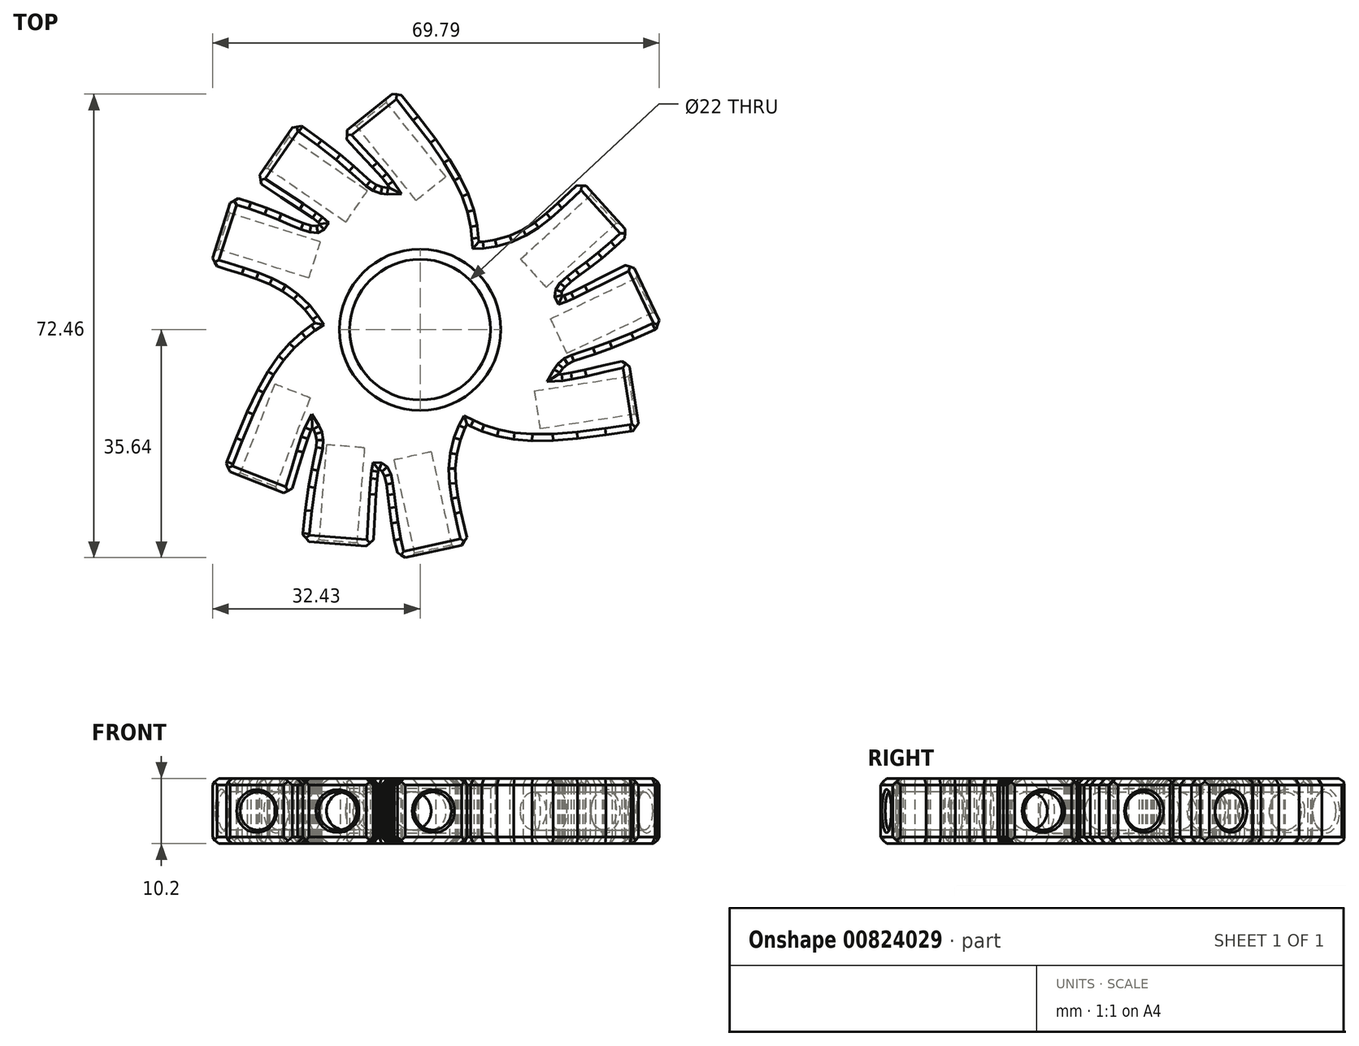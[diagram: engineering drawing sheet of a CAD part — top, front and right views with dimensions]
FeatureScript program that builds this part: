
annotation { "Feature Type Name" : "Feature", "Feature Type Description" : "" }
export const myFeature = defineFeature(function(context is Context, id is Id, definition is map)
    precondition{}
    {
        {
            var Q0;
            Q0=qCreatedBy(makeId("Top.planeOp"),FACE);
            var sketch = newSketch(context, id + "F0", { "sketchPlane" : qUnion([Q0])});
            skLineSegment(sketch, "E0", {"start": v(-3.87, -42.17) * mm, "end": v(8.83, -39.4) * mm});
            skLineSegment(sketch, "E1", {"start": v(8.83, -39.4) * mm, "end": v(8.67, -38.64) * mm});
            skLineSegment(sketch, "E2", {"start": v(8.67, -38.64) * mm, "end": v(8.17, -36.4) * mm});
            skLineSegment(sketch, "E3", {"start": v(8.17, -36.4) * mm, "end": v(7.52, -33.55) * mm});
            skLineSegment(sketch, "E4", {"start": v(7.52, -33.55) * mm, "end": v(6.96, -30.83) * mm});
            skLineSegment(sketch, "E5", {"start": v(6.96, -30.83) * mm, "end": v(6.6, -28.19) * mm});
            skLineSegment(sketch, "E6", {"start": v(6.6, -28.19) * mm, "end": v(6.48, -25.57) * mm});
            skLineSegment(sketch, "E7", {"start": v(6.48, -25.57) * mm, "end": v(6.72, -22.93) * mm});
            skLineSegment(sketch, "E8", {"start": v(6.72, -22.93) * mm, "end": v(7.4, -20.23) * mm});
            skLineSegment(sketch, "E9", {"start": v(7.4, -20.23) * mm, "end": v(8.24, -18.1) * mm});
            skLineSegment(sketch, "E10", {"start": v(8.24, -18.1) * mm, "end": v(8.6, -17.42) * mm});
            skLineSegment(sketch, "E11", {"start": v(8.6, -17.42) * mm, "end": v(9.26, -17.76) * mm});
            skLineSegment(sketch, "E12", {"start": v(9.26, -17.76) * mm, "end": v(11.34, -18.65) * mm});
            skLineSegment(sketch, "E13", {"start": v(11.34, -18.65) * mm, "end": v(14.16, -19.56) * mm});
            skLineSegment(sketch, "E14", {"start": v(14.16, -19.56) * mm, "end": v(17.2, -20.15) * mm});
            skLineSegment(sketch, "E15", {"start": v(17.2, -20.15) * mm, "end": v(20.6, -20.42) * mm});
            skLineSegment(sketch, "E16", {"start": v(20.6, -20.42) * mm, "end": v(24.46, -20.37) * mm});
            skLineSegment(sketch, "E17", {"start": v(24.46, -20.37) * mm, "end": v(28.95, -20.02) * mm});
            skLineSegment(sketch, "E18", {"start": v(28.95, -20.02) * mm, "end": v(34.19, -19.35) * mm});
            skLineSegment(sketch, "E19", {"start": v(34.19, -19.35) * mm, "end": v(38.78, -18.65) * mm});
            skLineSegment(sketch, "E20", {"start": v(38.78, -18.65) * mm, "end": v(40.3, -18.39) * mm});
            skLineSegment(sketch, "E21", {"start": v(40.3, -18.39) * mm, "end": v(38.33, -5.54) * mm});
            skLineSegment(sketch, "E22", {"start": v(38.33, -5.54) * mm, "end": v(37.16, -5.78) * mm});
            skLineSegment(sketch, "E23", {"start": v(37.16, -5.78) * mm, "end": v(33.7, -6.57) * mm});
            skLineSegment(sketch, "E24", {"start": v(33.7, -6.57) * mm, "end": v(30.3, -7.38) * mm});
            skLineSegment(sketch, "E25", {"start": v(30.3, -7.38) * mm, "end": v(27.7, -7.94) * mm});
            skLineSegment(sketch, "E26", {"start": v(27.7, -7.94) * mm, "end": v(26.02, -8.19) * mm});
            skLineSegment(sketch, "E27", {"start": v(26.02, -8.19) * mm, "end": v(25.45, -8.22) * mm});
            skLineSegment(sketch, "E28", {"start": v(25.45, -8.22) * mm, "end": v(25.62, -7.92) * mm});
            skLineSegment(sketch, "E29", {"start": v(25.62, -7.92) * mm, "end": v(26.22, -7.09) * mm});
            skLineSegment(sketch, "E30", {"start": v(26.22, -7.09) * mm, "end": v(27.1, -6.34) * mm});
            skLineSegment(sketch, "E31", {"start": v(27.1, -6.34) * mm, "end": v(28.29, -5.78) * mm});
            skLineSegment(sketch, "E32", {"start": v(28.29, -5.78) * mm, "end": v(29.92, -5.22) * mm});
            skLineSegment(sketch, "E33", {"start": v(29.92, -5.22) * mm, "end": v(32.2, -4.48) * mm});
            skLineSegment(sketch, "E34", {"start": v(32.2, -4.48) * mm, "end": v(35.26, -3.38) * mm});
            skLineSegment(sketch, "E35", {"start": v(35.26, -3.38) * mm, "end": v(39.3, -1.73) * mm});
            skLineSegment(sketch, "E36", {"start": v(39.3, -1.73) * mm, "end": v(43.18, 0.04) * mm});
            skLineSegment(sketch, "E37", {"start": v(43.18, 0.04) * mm, "end": v(44.46, 0.66) * mm});
            skLineSegment(sketch, "E38", {"start": v(44.46, 0.66) * mm, "end": v(38.88, 12.4) * mm});
            skLineSegment(sketch, "E39", {"start": v(38.88, 12.4) * mm, "end": v(37.64, 11.78) * mm});
            skLineSegment(sketch, "E40", {"start": v(37.64, 11.78) * mm, "end": v(33.94, 9.92) * mm});
            skLineSegment(sketch, "E41", {"start": v(33.94, 9.92) * mm, "end": v(30.3, 8.08) * mm});
            skLineSegment(sketch, "E42", {"start": v(30.3, 8.08) * mm, "end": v(27.73, 6.83) * mm});
            skLineSegment(sketch, "E43", {"start": v(27.73, 6.83) * mm, "end": v(26.49, 6.28) * mm});
            skLineSegment(sketch, "E44", {"start": v(26.49, 6.28) * mm, "end": v(26.06, 6.14) * mm});
            skLineSegment(sketch, "E45", {"start": v(26.06, 6.14) * mm, "end": v(25.98, 6.3) * mm});
            skLineSegment(sketch, "E46", {"start": v(25.98, 6.3) * mm, "end": v(26.03, 6.93) * mm});
            skLineSegment(sketch, "E47", {"start": v(26.03, 6.93) * mm, "end": v(26.62, 7.8) * mm});
            skLineSegment(sketch, "E48", {"start": v(26.62, 7.8) * mm, "end": v(27.73, 8.8) * mm});
            skLineSegment(sketch, "E49", {"start": v(27.73, 8.8) * mm, "end": v(29.3, 10) * mm});
            skLineSegment(sketch, "E50", {"start": v(29.3, 10) * mm, "end": v(31.24, 11.44) * mm});
            skLineSegment(sketch, "E51", {"start": v(31.24, 11.44) * mm, "end": v(33.46, 13.17) * mm});
            skLineSegment(sketch, "E52", {"start": v(33.46, 13.17) * mm, "end": v(35.89, 15.24) * mm});
            skLineSegment(sketch, "E53", {"start": v(35.89, 15.24) * mm, "end": v(37.83, 17.06) * mm});
            skLineSegment(sketch, "E54", {"start": v(37.83, 17.06) * mm, "end": v(38.44, 17.7) * mm});
            skLineSegment(sketch, "E55", {"start": v(38.44, 17.7) * mm, "end": v(29.69, 27.3) * mm});
            skLineSegment(sketch, "E56", {"start": v(29.69, 27.3) * mm, "end": v(29.11, 26.8) * mm});
            skLineSegment(sketch, "E57", {"start": v(29.11, 26.8) * mm, "end": v(27.42, 25.23) * mm});
            skLineSegment(sketch, "E58", {"start": v(27.42, 25.23) * mm, "end": v(25.28, 23.25) * mm});
            skLineSegment(sketch, "E59", {"start": v(25.28, 23.25) * mm, "end": v(23.2, 21.41) * mm});
            skLineSegment(sketch, "E60", {"start": v(23.2, 21.41) * mm, "end": v(21.1, 19.77) * mm});
            skLineSegment(sketch, "E61", {"start": v(21.1, 19.77) * mm, "end": v(18.89, 18.37) * mm});
            skLineSegment(sketch, "E62", {"start": v(18.89, 18.37) * mm, "end": v(16.48, 17.26) * mm});
            skLineSegment(sketch, "E63", {"start": v(16.48, 17.26) * mm, "end": v(13.8, 16.5) * mm});
            skLineSegment(sketch, "E64", {"start": v(13.8, 16.5) * mm, "end": v(11.53, 16.15) * mm});
            skLineSegment(sketch, "E65", {"start": v(11.53, 16.15) * mm, "end": v(10.77, 16.12) * mm});
            skLineSegment(sketch, "E66", {"start": v(10.77, 16.12) * mm, "end": v(10.73, 16.87) * mm});
            skLineSegment(sketch, "E67", {"start": v(10.73, 16.87) * mm, "end": v(10.47, 19.11) * mm});
            skLineSegment(sketch, "E68", {"start": v(10.47, 19.11) * mm, "end": v(9.84, 22.01) * mm});
            skLineSegment(sketch, "E69", {"start": v(9.84, 22.01) * mm, "end": v(8.83, 24.94) * mm});
            skLineSegment(sketch, "E70", {"start": v(8.83, 24.94) * mm, "end": v(7.37, 28) * mm});
            skLineSegment(sketch, "E71", {"start": v(7.37, 28) * mm, "end": v(5.4, 31.34) * mm});
            skLineSegment(sketch, "E72", {"start": v(5.4, 31.34) * mm, "end": v(2.84, 35.05) * mm});
            skLineSegment(sketch, "E73", {"start": v(2.84, 35.05) * mm, "end": v(-0.35, 39.25) * mm});
            skLineSegment(sketch, "E74", {"start": v(-0.35, 39.25) * mm, "end": v(-3.26, 42.87) * mm});
            skLineSegment(sketch, "E75", {"start": v(-3.26, 42.87) * mm, "end": v(-4.24, 44.06) * mm});
            skLineSegment(sketch, "E76", {"start": v(-4.24, 44.06) * mm, "end": v(-14.38, 35.92) * mm});
            skLineSegment(sketch, "E77", {"start": v(-14.38, 35.92) * mm, "end": v(-13.6, 35.04) * mm});
            skLineSegment(sketch, "E78", {"start": v(-13.6, 35.04) * mm, "end": v(-11.17, 32.43) * mm});
            skLineSegment(sketch, "E79", {"start": v(-11.17, 32.43) * mm, "end": v(-8.77, 29.9) * mm});
            skLineSegment(sketch, "E80", {"start": v(-8.77, 29.9) * mm, "end": v(-7, 27.93) * mm});
            skLineSegment(sketch, "E81", {"start": v(-7, 27.93) * mm, "end": v(-5.94, 26.59) * mm});
            skLineSegment(sketch, "E82", {"start": v(-5.94, 26.59) * mm, "end": v(-5.63, 26.11) * mm});
            skLineSegment(sketch, "E83", {"start": v(-5.63, 26.11) * mm, "end": v(-5.97, 26.1) * mm});
            skLineSegment(sketch, "E84", {"start": v(-5.97, 26.1) * mm, "end": v(-6.99, 26.21) * mm});
            skLineSegment(sketch, "E85", {"start": v(-6.99, 26.21) * mm, "end": v(-8.08, 26.6) * mm});
            skLineSegment(sketch, "E86", {"start": v(-8.08, 26.6) * mm, "end": v(-9.16, 27.35) * mm});
            skLineSegment(sketch, "E87", {"start": v(-9.16, 27.35) * mm, "end": v(-10.46, 28.5) * mm});
            skLineSegment(sketch, "E88", {"start": v(-10.46, 28.5) * mm, "end": v(-12.23, 30.09) * mm});
            skLineSegment(sketch, "E89", {"start": v(-12.23, 30.09) * mm, "end": v(-14.72, 32.2) * mm});
            skLineSegment(sketch, "E90", {"start": v(-14.72, 32.2) * mm, "end": v(-18.17, 34.86) * mm});
            skLineSegment(sketch, "E91", {"start": v(-18.17, 34.86) * mm, "end": v(-21.64, 37.35) * mm});
            skLineSegment(sketch, "E92", {"start": v(-21.64, 37.35) * mm, "end": v(-22.82, 38.14) * mm});
            skLineSegment(sketch, "E93", {"start": v(-22.82, 38.14) * mm, "end": v(-30.2, 27.43) * mm});
            skLineSegment(sketch, "E94", {"start": v(-30.2, 27.43) * mm, "end": v(-29.04, 26.67) * mm});
            skLineSegment(sketch, "E95", {"start": v(-29.04, 26.67) * mm, "end": v(-25.58, 24.4) * mm});
            skLineSegment(sketch, "E96", {"start": v(-25.58, 24.4) * mm, "end": v(-22.16, 22.16) * mm});
            skLineSegment(sketch, "E97", {"start": v(-22.16, 22.16) * mm, "end": v(-19.8, 20.56) * mm});
            skLineSegment(sketch, "E98", {"start": v(-19.8, 20.56) * mm, "end": v(-18.7, 19.76) * mm});
            skLineSegment(sketch, "E99", {"start": v(-18.7, 19.76) * mm, "end": v(-18.36, 19.46) * mm});
            skLineSegment(sketch, "E100", {"start": v(-18.36, 19.46) * mm, "end": v(-18.46, 19.31) * mm});
            skLineSegment(sketch, "E101", {"start": v(-18.46, 19.31) * mm, "end": v(-19.03, 19.04) * mm});
            skLineSegment(sketch, "E102", {"start": v(-19.03, 19.04) * mm, "end": v(-20.08, 19.11) * mm});
            skLineSegment(sketch, "E103", {"start": v(-20.08, 19.11) * mm, "end": v(-21.51, 19.58) * mm});
            skLineSegment(sketch, "E104", {"start": v(-21.51, 19.58) * mm, "end": v(-23.33, 20.34) * mm});
            skLineSegment(sketch, "E105", {"start": v(-23.33, 20.34) * mm, "end": v(-25.54, 21.3) * mm});
            skLineSegment(sketch, "E106", {"start": v(-25.54, 21.3) * mm, "end": v(-28.15, 22.36) * mm});
            skLineSegment(sketch, "E107", {"start": v(-28.15, 22.36) * mm, "end": v(-31.16, 23.43) * mm});
            skLineSegment(sketch, "E108", {"start": v(-31.16, 23.43) * mm, "end": v(-33.7, 24.2) * mm});
            skLineSegment(sketch, "E109", {"start": v(-33.7, 24.2) * mm, "end": v(-34.56, 24.4) * mm});
            skLineSegment(sketch, "E110", {"start": v(-34.56, 24.4) * mm, "end": v(-38.5, 12.02) * mm});
            skLineSegment(sketch, "E111", {"start": v(-38.5, 12.02) * mm, "end": v(-37.78, 11.78) * mm});
            skLineSegment(sketch, "E112", {"start": v(-37.78, 11.78) * mm, "end": v(-35.58, 11.1) * mm});
            skLineSegment(sketch, "E113", {"start": v(-35.58, 11.1) * mm, "end": v(-32.8, 10.23) * mm});
            skLineSegment(sketch, "E114", {"start": v(-32.8, 10.23) * mm, "end": v(-30.16, 9.35) * mm});
            skLineSegment(sketch, "E115", {"start": v(-30.16, 9.35) * mm, "end": v(-27.69, 8.35) * mm});
            skLineSegment(sketch, "E116", {"start": v(-27.69, 8.35) * mm, "end": v(-25.36, 7.14) * mm});
            skLineSegment(sketch, "E117", {"start": v(-25.36, 7.14) * mm, "end": v(-23.2, 5.61) * mm});
            skLineSegment(sketch, "E118", {"start": v(-23.2, 5.61) * mm, "end": v(-21.2, 3.68) * mm});
            skLineSegment(sketch, "E119", {"start": v(-21.2, 3.68) * mm, "end": v(-19.77, 1.88) * mm});
            skLineSegment(sketch, "E120", {"start": v(-19.77, 1.88) * mm, "end": v(-19.36, 1.24) * mm});
            skLineSegment(sketch, "E121", {"start": v(-19.36, 1.24) * mm, "end": v(-20, 0.83) * mm});
            skLineSegment(sketch, "E122", {"start": v(-20, 0.83) * mm, "end": v(-21.8, -0.52) * mm});
            skLineSegment(sketch, "E123", {"start": v(-21.8, -0.52) * mm, "end": v(-24, -2.52) * mm});
            skLineSegment(sketch, "E124", {"start": v(-24, -2.52) * mm, "end": v(-26.03, -4.86) * mm});
            skLineSegment(sketch, "E125", {"start": v(-26.03, -4.86) * mm, "end": v(-27.96, -7.66) * mm});
            skLineSegment(sketch, "E126", {"start": v(-27.96, -7.66) * mm, "end": v(-29.85, -11.03) * mm});
            skLineSegment(sketch, "E127", {"start": v(-29.85, -11.03) * mm, "end": v(-31.79, -15.1) * mm});
            skLineSegment(sketch, "E128", {"start": v(-31.79, -15.1) * mm, "end": v(-33.83, -19.96) * mm});
            skLineSegment(sketch, "E129", {"start": v(-33.83, -19.96) * mm, "end": v(-35.51, -24.3) * mm});
            skLineSegment(sketch, "E130", {"start": v(-35.51, -24.3) * mm, "end": v(-36.05, -25.74) * mm});
            skLineSegment(sketch, "E131", {"start": v(-36.05, -25.74) * mm, "end": v(-23.94, -30.45) * mm});
            skLineSegment(sketch, "E132", {"start": v(-23.94, -30.45) * mm, "end": v(-23.57, -29.33) * mm});
            skLineSegment(sketch, "E133", {"start": v(-23.57, -29.33) * mm, "end": v(-22.52, -25.92) * mm});
            skLineSegment(sketch, "E134", {"start": v(-22.52, -25.92) * mm, "end": v(-21.52, -22.58) * mm});
            skLineSegment(sketch, "E135", {"start": v(-21.52, -22.58) * mm, "end": v(-20.7, -20.06) * mm});
            skLineSegment(sketch, "E136", {"start": v(-20.7, -20.06) * mm, "end": v(-20.07, -18.47) * mm});
            skLineSegment(sketch, "E137", {"start": v(-20.07, -18.47) * mm, "end": v(-19.82, -17.97) * mm});
            skLineSegment(sketch, "E138", {"start": v(-19.82, -17.97) * mm, "end": v(-19.64, -18.26) * mm});
            skLineSegment(sketch, "E139", {"start": v(-19.64, -18.26) * mm, "end": v(-19.23, -19.2) * mm});
            skLineSegment(sketch, "E140", {"start": v(-19.23, -19.2) * mm, "end": v(-19.02, -20.34) * mm});
            skLineSegment(sketch, "E141", {"start": v(-19.02, -20.34) * mm, "end": v(-19.12, -21.64) * mm});
            skLineSegment(sketch, "E142", {"start": v(-19.12, -21.64) * mm, "end": v(-19.46, -23.34) * mm});
            skLineSegment(sketch, "E143", {"start": v(-19.46, -23.34) * mm, "end": v(-19.96, -25.67) * mm});
            skLineSegment(sketch, "E144", {"start": v(-19.96, -25.67) * mm, "end": v(-20.53, -28.88) * mm});
            skLineSegment(sketch, "E145", {"start": v(-20.53, -28.88) * mm, "end": v(-21.12, -33.2) * mm});
            skLineSegment(sketch, "E146", {"start": v(-21.12, -33.2) * mm, "end": v(-21.54, -37.45) * mm});
            skLineSegment(sketch, "E147", {"start": v(-21.54, -37.45) * mm, "end": v(-21.64, -38.87) * mm});
            skLineSegment(sketch, "E148", {"start": v(-21.64, -38.87) * mm, "end": v(-8.68, -39.9) * mm});
            skLineSegment(sketch, "E149", {"start": v(-8.68, -39.9) * mm, "end": v(-8.6, -38.52) * mm});
            skLineSegment(sketch, "E150", {"start": v(-8.6, -38.52) * mm, "end": v(-8.36, -34.39) * mm});
            skLineSegment(sketch, "E151", {"start": v(-8.36, -34.39) * mm, "end": v(-8.13, -30.3) * mm});
            skLineSegment(sketch, "E152", {"start": v(-8.13, -30.3) * mm, "end": v(-7.92, -27.46) * mm});
            skLineSegment(sketch, "E153", {"start": v(-7.92, -27.46) * mm, "end": v(-7.78, -26.11) * mm});
            skLineSegment(sketch, "E154", {"start": v(-7.78, -26.11) * mm, "end": v(-7.69, -25.67) * mm});
            skLineSegment(sketch, "E155", {"start": v(-7.69, -25.67) * mm, "end": v(-7.51, -25.68) * mm});
            skLineSegment(sketch, "E156", {"start": v(-7.51, -25.68) * mm, "end": v(-7, -26.04) * mm});
            skLineSegment(sketch, "E157", {"start": v(-7, -26.04) * mm, "end": v(-6.53, -26.98) * mm});
            skLineSegment(sketch, "E158", {"start": v(-6.53, -26.98) * mm, "end": v(-6.22, -28.45) * mm});
            skLineSegment(sketch, "E159", {"start": v(-6.22, -28.45) * mm, "end": v(-5.96, -30.41) * mm});
            skLineSegment(sketch, "E160", {"start": v(-5.96, -30.41) * mm, "end": v(-5.69, -32.8) * mm});
            skLineSegment(sketch, "E161", {"start": v(-5.69, -32.8) * mm, "end": v(-5.3, -35.6) * mm});
            skLineSegment(sketch, "E162", {"start": v(-5.3, -35.6) * mm, "end": v(-4.73, -38.73) * mm});
            skLineSegment(sketch, "E163", {"start": v(-4.73, -38.73) * mm, "end": v(-4.12, -41.32) * mm});
            skLineSegment(sketch, "E164", {"start": v(-4.12, -41.32) * mm, "end": v(-3.87, -42.17) * mm});
            skCircle(sketch, "E165", {"center": v(0, 0) * mm, "radius": 11 * mm});
            skSolve(sketch);
        }
        {
            var Q0;
            Q0=makeQuery(id+"F0.imprint","IMPRINT",FACE,{"disambiguationData":[TD([[makeQuery(id+"F0.imprint","IMPRINT",EDGE,{"derivedFrom":sQuery(id+"F0.wireOp",EDGE,"E0")}),1.0]])]});
            var Q1;
            Q1=makeQuery(id+"F0.imprint","IMPRINT",FACE,{"disambiguationData":[TD([[makeQuery(id+"F0.imprint","IMPRINT",EDGE,{"derivedFrom":sQuery(id+"F0.wireOp",EDGE,"E165")}),1.0]])]});
            extrude(context, id + "F1", {"entities" : qUnion([Q0, Q1]), "endBound" : BoundingType.SYMMETRIC, "depth" : 12 * mm, "offsetDistance" : 25 * mm});
        }
        {
            var Q0;
            Q0=makeQuery(id+"F1.opExtrude","CAP_FACE",FACE,{"disambiguationData":[OSD([sQuery(id+"F0.wireOp",EDGE,"E0"),sQuery(id+"F0.wireOp",EDGE,"E1"),sQuery(id+"F0.wireOp",EDGE,"E2"),sQuery(id+"F0.wireOp",EDGE,"E3"),sQuery(id+"F0.wireOp",EDGE,"E4"),sQuery(id+"F0.wireOp",EDGE,"E5"),sQuery(id+"F0.wireOp",EDGE,"E6"),sQuery(id+"F0.wireOp",EDGE,"E7"),sQuery(id+"F0.wireOp",EDGE,"E8"),sQuery(id+"F0.wireOp",EDGE,"E9"),sQuery(id+"F0.wireOp",EDGE,"E10"),sQuery(id+"F0.wireOp",EDGE,"E11"),sQuery(id+"F0.wireOp",EDGE,"E12"),sQuery(id+"F0.wireOp",EDGE,"E13"),sQuery(id+"F0.wireOp",EDGE,"E14"),sQuery(id+"F0.wireOp",EDGE,"E15"),sQuery(id+"F0.wireOp",EDGE,"E16"),sQuery(id+"F0.wireOp",EDGE,"E17"),sQuery(id+"F0.wireOp",EDGE,"E18"),sQuery(id+"F0.wireOp",EDGE,"E19"),sQuery(id+"F0.wireOp",EDGE,"E20"),sQuery(id+"F0.wireOp",EDGE,"E21"),sQuery(id+"F0.wireOp",EDGE,"E22"),sQuery(id+"F0.wireOp",EDGE,"E23"),sQuery(id+"F0.wireOp",EDGE,"E24"),sQuery(id+"F0.wireOp",EDGE,"E25"),sQuery(id+"F0.wireOp",EDGE,"E26"),sQuery(id+"F0.wireOp",EDGE,"E27"),sQuery(id+"F0.wireOp",EDGE,"E28"),sQuery(id+"F0.wireOp",EDGE,"E29"),sQuery(id+"F0.wireOp",EDGE,"E30"),sQuery(id+"F0.wireOp",EDGE,"E31"),sQuery(id+"F0.wireOp",EDGE,"E32"),sQuery(id+"F0.wireOp",EDGE,"E33"),sQuery(id+"F0.wireOp",EDGE,"E34"),sQuery(id+"F0.wireOp",EDGE,"E35"),sQuery(id+"F0.wireOp",EDGE,"E36"),sQuery(id+"F0.wireOp",EDGE,"E37"),sQuery(id+"F0.wireOp",EDGE,"E38"),sQuery(id+"F0.wireOp",EDGE,"E39"),sQuery(id+"F0.wireOp",EDGE,"E40"),sQuery(id+"F0.wireOp",EDGE,"E41"),sQuery(id+"F0.wireOp",EDGE,"E42"),sQuery(id+"F0.wireOp",EDGE,"E43"),sQuery(id+"F0.wireOp",EDGE,"E44"),sQuery(id+"F0.wireOp",EDGE,"E45"),sQuery(id+"F0.wireOp",EDGE,"E46"),sQuery(id+"F0.wireOp",EDGE,"E47"),sQuery(id+"F0.wireOp",EDGE,"E48"),sQuery(id+"F0.wireOp",EDGE,"E49"),sQuery(id+"F0.wireOp",EDGE,"E50"),sQuery(id+"F0.wireOp",EDGE,"E51"),sQuery(id+"F0.wireOp",EDGE,"E52"),sQuery(id+"F0.wireOp",EDGE,"E53"),sQuery(id+"F0.wireOp",EDGE,"E54"),sQuery(id+"F0.wireOp",EDGE,"E55"),sQuery(id+"F0.wireOp",EDGE,"E56"),sQuery(id+"F0.wireOp",EDGE,"E57"),sQuery(id+"F0.wireOp",EDGE,"E58"),sQuery(id+"F0.wireOp",EDGE,"E59"),sQuery(id+"F0.wireOp",EDGE,"E60"),sQuery(id+"F0.wireOp",EDGE,"E61"),sQuery(id+"F0.wireOp",EDGE,"E62"),sQuery(id+"F0.wireOp",EDGE,"E63"),sQuery(id+"F0.wireOp",EDGE,"E64"),sQuery(id+"F0.wireOp",EDGE,"E65"),sQuery(id+"F0.wireOp",EDGE,"E66"),sQuery(id+"F0.wireOp",EDGE,"E67"),sQuery(id+"F0.wireOp",EDGE,"E68"),sQuery(id+"F0.wireOp",EDGE,"E69"),sQuery(id+"F0.wireOp",EDGE,"E70"),sQuery(id+"F0.wireOp",EDGE,"E71"),sQuery(id+"F0.wireOp",EDGE,"E72"),sQuery(id+"F0.wireOp",EDGE,"E73"),sQuery(id+"F0.wireOp",EDGE,"E74"),sQuery(id+"F0.wireOp",EDGE,"E75"),sQuery(id+"F0.wireOp",EDGE,"E76"),sQuery(id+"F0.wireOp",EDGE,"E77"),sQuery(id+"F0.wireOp",EDGE,"E78"),sQuery(id+"F0.wireOp",EDGE,"E79"),sQuery(id+"F0.wireOp",EDGE,"E80"),sQuery(id+"F0.wireOp",EDGE,"E81"),sQuery(id+"F0.wireOp",EDGE,"E82"),sQuery(id+"F0.wireOp",EDGE,"E83"),sQuery(id+"F0.wireOp",EDGE,"E84"),sQuery(id+"F0.wireOp",EDGE,"E85"),sQuery(id+"F0.wireOp",EDGE,"E86"),sQuery(id+"F0.wireOp",EDGE,"E87"),sQuery(id+"F0.wireOp",EDGE,"E88"),sQuery(id+"F0.wireOp",EDGE,"E89"),sQuery(id+"F0.wireOp",EDGE,"E90"),sQuery(id+"F0.wireOp",EDGE,"E91"),sQuery(id+"F0.wireOp",EDGE,"E92"),sQuery(id+"F0.wireOp",EDGE,"E93"),sQuery(id+"F0.wireOp",EDGE,"E94"),sQuery(id+"F0.wireOp",EDGE,"E95"),sQuery(id+"F0.wireOp",EDGE,"E96"),sQuery(id+"F0.wireOp",EDGE,"E97"),sQuery(id+"F0.wireOp",EDGE,"E98"),sQuery(id+"F0.wireOp",EDGE,"E99"),sQuery(id+"F0.wireOp",EDGE,"E100"),sQuery(id+"F0.wireOp",EDGE,"E101"),sQuery(id+"F0.wireOp",EDGE,"E102"),sQuery(id+"F0.wireOp",EDGE,"E103"),sQuery(id+"F0.wireOp",EDGE,"E104"),sQuery(id+"F0.wireOp",EDGE,"E105"),sQuery(id+"F0.wireOp",EDGE,"E106"),sQuery(id+"F0.wireOp",EDGE,"E107"),sQuery(id+"F0.wireOp",EDGE,"E108"),sQuery(id+"F0.wireOp",EDGE,"E109"),sQuery(id+"F0.wireOp",EDGE,"E110"),sQuery(id+"F0.wireOp",EDGE,"E111"),sQuery(id+"F0.wireOp",EDGE,"E112"),sQuery(id+"F0.wireOp",EDGE,"E113"),sQuery(id+"F0.wireOp",EDGE,"E114"),sQuery(id+"F0.wireOp",EDGE,"E115"),sQuery(id+"F0.wireOp",EDGE,"E116"),sQuery(id+"F0.wireOp",EDGE,"E117"),sQuery(id+"F0.wireOp",EDGE,"E118"),sQuery(id+"F0.wireOp",EDGE,"E119"),sQuery(id+"F0.wireOp",EDGE,"E120"),sQuery(id+"F0.wireOp",EDGE,"E121"),sQuery(id+"F0.wireOp",EDGE,"E122"),sQuery(id+"F0.wireOp",EDGE,"E123"),sQuery(id+"F0.wireOp",EDGE,"E124"),sQuery(id+"F0.wireOp",EDGE,"E125"),sQuery(id+"F0.wireOp",EDGE,"E126"),sQuery(id+"F0.wireOp",EDGE,"E127"),sQuery(id+"F0.wireOp",EDGE,"E128"),sQuery(id+"F0.wireOp",EDGE,"E129"),sQuery(id+"F0.wireOp",EDGE,"E130"),sQuery(id+"F0.wireOp",EDGE,"E131"),sQuery(id+"F0.wireOp",EDGE,"E132"),sQuery(id+"F0.wireOp",EDGE,"E133"),sQuery(id+"F0.wireOp",EDGE,"E134"),sQuery(id+"F0.wireOp",EDGE,"E135"),sQuery(id+"F0.wireOp",EDGE,"E136"),sQuery(id+"F0.wireOp",EDGE,"E137"),sQuery(id+"F0.wireOp",EDGE,"E138"),sQuery(id+"F0.wireOp",EDGE,"E139"),sQuery(id+"F0.wireOp",EDGE,"E140"),sQuery(id+"F0.wireOp",EDGE,"E141"),sQuery(id+"F0.wireOp",EDGE,"E142"),sQuery(id+"F0.wireOp",EDGE,"E143"),sQuery(id+"F0.wireOp",EDGE,"E144"),sQuery(id+"F0.wireOp",EDGE,"E145"),sQuery(id+"F0.wireOp",EDGE,"E146"),sQuery(id+"F0.wireOp",EDGE,"E147"),sQuery(id+"F0.wireOp",EDGE,"E148"),sQuery(id+"F0.wireOp",EDGE,"E149"),sQuery(id+"F0.wireOp",EDGE,"E150"),sQuery(id+"F0.wireOp",EDGE,"E151"),sQuery(id+"F0.wireOp",EDGE,"E152"),sQuery(id+"F0.wireOp",EDGE,"E153"),sQuery(id+"F0.wireOp",EDGE,"E154"),sQuery(id+"F0.wireOp",EDGE,"E155"),sQuery(id+"F0.wireOp",EDGE,"E156"),sQuery(id+"F0.wireOp",EDGE,"E157"),sQuery(id+"F0.wireOp",EDGE,"E158"),sQuery(id+"F0.wireOp",EDGE,"E159"),sQuery(id+"F0.wireOp",EDGE,"E160"),sQuery(id+"F0.wireOp",EDGE,"E161"),sQuery(id+"F0.wireOp",EDGE,"E162"),sQuery(id+"F0.wireOp",EDGE,"E163"),sQuery(id+"F0.wireOp",EDGE,"E164"),sQuery(id+"F0.wireOp",EDGE,"E165")])],"isStart":false});
            var Q1;
            Q1=makeQuery(id+"F1.opExtrude","CAP_FACE",FACE,{"disambiguationData":[OSD([sQuery(id+"F0.wireOp",EDGE,"E0"),sQuery(id+"F0.wireOp",EDGE,"E1"),sQuery(id+"F0.wireOp",EDGE,"E2"),sQuery(id+"F0.wireOp",EDGE,"E3"),sQuery(id+"F0.wireOp",EDGE,"E4"),sQuery(id+"F0.wireOp",EDGE,"E5"),sQuery(id+"F0.wireOp",EDGE,"E6"),sQuery(id+"F0.wireOp",EDGE,"E7"),sQuery(id+"F0.wireOp",EDGE,"E8"),sQuery(id+"F0.wireOp",EDGE,"E9"),sQuery(id+"F0.wireOp",EDGE,"E10"),sQuery(id+"F0.wireOp",EDGE,"E11"),sQuery(id+"F0.wireOp",EDGE,"E12"),sQuery(id+"F0.wireOp",EDGE,"E13"),sQuery(id+"F0.wireOp",EDGE,"E14"),sQuery(id+"F0.wireOp",EDGE,"E15"),sQuery(id+"F0.wireOp",EDGE,"E16"),sQuery(id+"F0.wireOp",EDGE,"E17"),sQuery(id+"F0.wireOp",EDGE,"E18"),sQuery(id+"F0.wireOp",EDGE,"E19"),sQuery(id+"F0.wireOp",EDGE,"E20"),sQuery(id+"F0.wireOp",EDGE,"E21"),sQuery(id+"F0.wireOp",EDGE,"E22"),sQuery(id+"F0.wireOp",EDGE,"E23"),sQuery(id+"F0.wireOp",EDGE,"E24"),sQuery(id+"F0.wireOp",EDGE,"E25"),sQuery(id+"F0.wireOp",EDGE,"E26"),sQuery(id+"F0.wireOp",EDGE,"E27"),sQuery(id+"F0.wireOp",EDGE,"E28"),sQuery(id+"F0.wireOp",EDGE,"E29"),sQuery(id+"F0.wireOp",EDGE,"E30"),sQuery(id+"F0.wireOp",EDGE,"E31"),sQuery(id+"F0.wireOp",EDGE,"E32"),sQuery(id+"F0.wireOp",EDGE,"E33"),sQuery(id+"F0.wireOp",EDGE,"E34"),sQuery(id+"F0.wireOp",EDGE,"E35"),sQuery(id+"F0.wireOp",EDGE,"E36"),sQuery(id+"F0.wireOp",EDGE,"E37"),sQuery(id+"F0.wireOp",EDGE,"E38"),sQuery(id+"F0.wireOp",EDGE,"E39"),sQuery(id+"F0.wireOp",EDGE,"E40"),sQuery(id+"F0.wireOp",EDGE,"E41"),sQuery(id+"F0.wireOp",EDGE,"E42"),sQuery(id+"F0.wireOp",EDGE,"E43"),sQuery(id+"F0.wireOp",EDGE,"E44"),sQuery(id+"F0.wireOp",EDGE,"E45"),sQuery(id+"F0.wireOp",EDGE,"E46"),sQuery(id+"F0.wireOp",EDGE,"E47"),sQuery(id+"F0.wireOp",EDGE,"E48"),sQuery(id+"F0.wireOp",EDGE,"E49"),sQuery(id+"F0.wireOp",EDGE,"E50"),sQuery(id+"F0.wireOp",EDGE,"E51"),sQuery(id+"F0.wireOp",EDGE,"E52"),sQuery(id+"F0.wireOp",EDGE,"E53"),sQuery(id+"F0.wireOp",EDGE,"E54"),sQuery(id+"F0.wireOp",EDGE,"E55"),sQuery(id+"F0.wireOp",EDGE,"E56"),sQuery(id+"F0.wireOp",EDGE,"E57"),sQuery(id+"F0.wireOp",EDGE,"E58"),sQuery(id+"F0.wireOp",EDGE,"E59"),sQuery(id+"F0.wireOp",EDGE,"E60"),sQuery(id+"F0.wireOp",EDGE,"E61"),sQuery(id+"F0.wireOp",EDGE,"E62"),sQuery(id+"F0.wireOp",EDGE,"E63"),sQuery(id+"F0.wireOp",EDGE,"E64"),sQuery(id+"F0.wireOp",EDGE,"E65"),sQuery(id+"F0.wireOp",EDGE,"E66"),sQuery(id+"F0.wireOp",EDGE,"E67"),sQuery(id+"F0.wireOp",EDGE,"E68"),sQuery(id+"F0.wireOp",EDGE,"E69"),sQuery(id+"F0.wireOp",EDGE,"E70"),sQuery(id+"F0.wireOp",EDGE,"E71"),sQuery(id+"F0.wireOp",EDGE,"E72"),sQuery(id+"F0.wireOp",EDGE,"E73"),sQuery(id+"F0.wireOp",EDGE,"E74"),sQuery(id+"F0.wireOp",EDGE,"E75"),sQuery(id+"F0.wireOp",EDGE,"E76"),sQuery(id+"F0.wireOp",EDGE,"E77"),sQuery(id+"F0.wireOp",EDGE,"E78"),sQuery(id+"F0.wireOp",EDGE,"E79"),sQuery(id+"F0.wireOp",EDGE,"E80"),sQuery(id+"F0.wireOp",EDGE,"E81"),sQuery(id+"F0.wireOp",EDGE,"E82"),sQuery(id+"F0.wireOp",EDGE,"E83"),sQuery(id+"F0.wireOp",EDGE,"E84"),sQuery(id+"F0.wireOp",EDGE,"E85"),sQuery(id+"F0.wireOp",EDGE,"E86"),sQuery(id+"F0.wireOp",EDGE,"E87"),sQuery(id+"F0.wireOp",EDGE,"E88"),sQuery(id+"F0.wireOp",EDGE,"E89"),sQuery(id+"F0.wireOp",EDGE,"E90"),sQuery(id+"F0.wireOp",EDGE,"E91"),sQuery(id+"F0.wireOp",EDGE,"E92"),sQuery(id+"F0.wireOp",EDGE,"E93"),sQuery(id+"F0.wireOp",EDGE,"E94"),sQuery(id+"F0.wireOp",EDGE,"E95"),sQuery(id+"F0.wireOp",EDGE,"E96"),sQuery(id+"F0.wireOp",EDGE,"E97"),sQuery(id+"F0.wireOp",EDGE,"E98"),sQuery(id+"F0.wireOp",EDGE,"E99"),sQuery(id+"F0.wireOp",EDGE,"E100"),sQuery(id+"F0.wireOp",EDGE,"E101"),sQuery(id+"F0.wireOp",EDGE,"E102"),sQuery(id+"F0.wireOp",EDGE,"E103"),sQuery(id+"F0.wireOp",EDGE,"E104"),sQuery(id+"F0.wireOp",EDGE,"E105"),sQuery(id+"F0.wireOp",EDGE,"E106"),sQuery(id+"F0.wireOp",EDGE,"E107"),sQuery(id+"F0.wireOp",EDGE,"E108"),sQuery(id+"F0.wireOp",EDGE,"E109"),sQuery(id+"F0.wireOp",EDGE,"E110"),sQuery(id+"F0.wireOp",EDGE,"E111"),sQuery(id+"F0.wireOp",EDGE,"E112"),sQuery(id+"F0.wireOp",EDGE,"E113"),sQuery(id+"F0.wireOp",EDGE,"E114"),sQuery(id+"F0.wireOp",EDGE,"E115"),sQuery(id+"F0.wireOp",EDGE,"E116"),sQuery(id+"F0.wireOp",EDGE,"E117"),sQuery(id+"F0.wireOp",EDGE,"E118"),sQuery(id+"F0.wireOp",EDGE,"E119"),sQuery(id+"F0.wireOp",EDGE,"E120"),sQuery(id+"F0.wireOp",EDGE,"E121"),sQuery(id+"F0.wireOp",EDGE,"E122"),sQuery(id+"F0.wireOp",EDGE,"E123"),sQuery(id+"F0.wireOp",EDGE,"E124"),sQuery(id+"F0.wireOp",EDGE,"E125"),sQuery(id+"F0.wireOp",EDGE,"E126"),sQuery(id+"F0.wireOp",EDGE,"E127"),sQuery(id+"F0.wireOp",EDGE,"E128"),sQuery(id+"F0.wireOp",EDGE,"E129"),sQuery(id+"F0.wireOp",EDGE,"E130"),sQuery(id+"F0.wireOp",EDGE,"E131"),sQuery(id+"F0.wireOp",EDGE,"E132"),sQuery(id+"F0.wireOp",EDGE,"E133"),sQuery(id+"F0.wireOp",EDGE,"E134"),sQuery(id+"F0.wireOp",EDGE,"E135"),sQuery(id+"F0.wireOp",EDGE,"E136"),sQuery(id+"F0.wireOp",EDGE,"E137"),sQuery(id+"F0.wireOp",EDGE,"E138"),sQuery(id+"F0.wireOp",EDGE,"E139"),sQuery(id+"F0.wireOp",EDGE,"E140"),sQuery(id+"F0.wireOp",EDGE,"E141"),sQuery(id+"F0.wireOp",EDGE,"E142"),sQuery(id+"F0.wireOp",EDGE,"E143"),sQuery(id+"F0.wireOp",EDGE,"E144"),sQuery(id+"F0.wireOp",EDGE,"E145"),sQuery(id+"F0.wireOp",EDGE,"E146"),sQuery(id+"F0.wireOp",EDGE,"E147"),sQuery(id+"F0.wireOp",EDGE,"E148"),sQuery(id+"F0.wireOp",EDGE,"E149"),sQuery(id+"F0.wireOp",EDGE,"E150"),sQuery(id+"F0.wireOp",EDGE,"E151"),sQuery(id+"F0.wireOp",EDGE,"E152"),sQuery(id+"F0.wireOp",EDGE,"E153"),sQuery(id+"F0.wireOp",EDGE,"E154"),sQuery(id+"F0.wireOp",EDGE,"E155"),sQuery(id+"F0.wireOp",EDGE,"E156"),sQuery(id+"F0.wireOp",EDGE,"E157"),sQuery(id+"F0.wireOp",EDGE,"E158"),sQuery(id+"F0.wireOp",EDGE,"E159"),sQuery(id+"F0.wireOp",EDGE,"E160"),sQuery(id+"F0.wireOp",EDGE,"E161"),sQuery(id+"F0.wireOp",EDGE,"E162"),sQuery(id+"F0.wireOp",EDGE,"E163"),sQuery(id+"F0.wireOp",EDGE,"E164"),sQuery(id+"F0.wireOp",EDGE,"E165")])],"isStart":true});
            chamfer(context, id + "F2", {"entities" : qUnion([Q0, Q1]), "width" : 1.2 * mm, "tangentPropagation" : true});
        }
        {
            var Q0;
            Q0=makeQuery(id+"F1.opExtrude","SWEPT_EDGE",EDGE,{"disambiguationData":[OSD([sQuery(id+"F0.wireOp",EDGE,"E147"),sQuery(id+"F0.wireOp",EDGE,"E148")])]});
            var Q1;
            Q1=makeQuery(id+"F1.opExtrude","SWEPT_EDGE",EDGE,{"disambiguationData":[OSD([sQuery(id+"F0.wireOp",EDGE,"E148"),sQuery(id+"F0.wireOp",EDGE,"E149")])]});
            var Q2;
            Q2=makeQuery(id+"F1.opExtrude","SWEPT_EDGE",EDGE,{"disambiguationData":[OSD([sQuery(id+"F0.wireOp",EDGE,"E0"),sQuery(id+"F0.wireOp",EDGE,"E164")])]});
            var Q3;
            Q3=makeQuery(id+"F1.opExtrude","SWEPT_EDGE",EDGE,{"disambiguationData":[OSD([sQuery(id+"F0.wireOp",EDGE,"E0"),sQuery(id+"F0.wireOp",EDGE,"E1")])]});
            var Q4;
            Q4=makeQuery(id+"F1.opExtrude","SWEPT_EDGE",EDGE,{"disambiguationData":[OSD([sQuery(id+"F0.wireOp",EDGE,"E130"),sQuery(id+"F0.wireOp",EDGE,"E131")])]});
            var Q5;
            Q5=makeQuery(id+"F1.opExtrude","SWEPT_EDGE",EDGE,{"disambiguationData":[OSD([sQuery(id+"F0.wireOp",EDGE,"E131"),sQuery(id+"F0.wireOp",EDGE,"E132")])]});
            var Q6;
            Q6=makeQuery(id+"F1.opExtrude","SWEPT_EDGE",EDGE,{"disambiguationData":[OSD([sQuery(id+"F0.wireOp",EDGE,"E20"),sQuery(id+"F0.wireOp",EDGE,"E21")])]});
            var Q7;
            Q7=makeQuery(id+"F1.opExtrude","SWEPT_EDGE",EDGE,{"disambiguationData":[OSD([sQuery(id+"F0.wireOp",EDGE,"E21"),sQuery(id+"F0.wireOp",EDGE,"E22")])]});
            var Q8;
            Q8=makeQuery(id+"F1.opExtrude","SWEPT_EDGE",EDGE,{"disambiguationData":[OSD([sQuery(id+"F0.wireOp",EDGE,"E37"),sQuery(id+"F0.wireOp",EDGE,"E38")])]});
            var Q9;
            Q9=makeQuery(id+"F1.opExtrude","SWEPT_EDGE",EDGE,{"disambiguationData":[OSD([sQuery(id+"F0.wireOp",EDGE,"E38"),sQuery(id+"F0.wireOp",EDGE,"E39")])]});
            var Q10;
            Q10=makeQuery(id+"F1.opExtrude","SWEPT_EDGE",EDGE,{"disambiguationData":[OSD([sQuery(id+"F0.wireOp",EDGE,"E54"),sQuery(id+"F0.wireOp",EDGE,"E55")])]});
            var Q11;
            Q11=makeQuery(id+"F1.opExtrude","SWEPT_EDGE",EDGE,{"disambiguationData":[OSD([sQuery(id+"F0.wireOp",EDGE,"E55"),sQuery(id+"F0.wireOp",EDGE,"E56")])]});
            var Q12;
            Q12=makeQuery(id+"F1.opExtrude","SWEPT_EDGE",EDGE,{"disambiguationData":[OSD([sQuery(id+"F0.wireOp",EDGE,"E75"),sQuery(id+"F0.wireOp",EDGE,"E76")])]});
            var Q13;
            Q13=makeQuery(id+"F1.opExtrude","SWEPT_EDGE",EDGE,{"disambiguationData":[OSD([sQuery(id+"F0.wireOp",EDGE,"E76"),sQuery(id+"F0.wireOp",EDGE,"E77")])]});
            var Q14;
            Q14=makeQuery(id+"F1.opExtrude","SWEPT_EDGE",EDGE,{"disambiguationData":[OSD([sQuery(id+"F0.wireOp",EDGE,"E92"),sQuery(id+"F0.wireOp",EDGE,"E93")])]});
            var Q15;
            Q15=makeQuery(id+"F1.opExtrude","SWEPT_EDGE",EDGE,{"disambiguationData":[OSD([sQuery(id+"F0.wireOp",EDGE,"E93"),sQuery(id+"F0.wireOp",EDGE,"E94")])]});
            var Q16;
            Q16=makeQuery(id+"F1.opExtrude","SWEPT_EDGE",EDGE,{"disambiguationData":[OSD([sQuery(id+"F0.wireOp",EDGE,"E109"),sQuery(id+"F0.wireOp",EDGE,"E110")])]});
            var Q17;
            Q17=makeQuery(id+"F1.opExtrude","SWEPT_EDGE",EDGE,{"disambiguationData":[OSD([sQuery(id+"F0.wireOp",EDGE,"E110"),sQuery(id+"F0.wireOp",EDGE,"E111")])]});
            chamfer(context, id + "F3", {"entities" : qUnion([Q0, Q1, Q2, Q3, Q4, Q5, Q6, Q7, Q8, Q9, Q10, Q11, Q12, Q13, Q14, Q15, Q16, Q17]), "width" : 1.2 * mm, "tangentPropagation" : true});
        }
        {
            var Q0;
            Q0=makeQuery(id+"F1.opExtrude","SWEPT_FACE",FACE,{"disambiguationData":[OSD([sQuery(id+"F0.wireOp",EDGE,"E76")])]});
            var sketch = newSketch(context, id + "F4", { "sketchPlane" : qUnion([Q0])});
            skLineSegment(sketch, "E166", {"start": v(-23.07, 0) * mm, "end": v(-12.55, 0) * mm, "construction": true});
            skLineSegment(sketch, "E167", {"start": v(-17.81, 4.8) * mm, "end": v(-17.81, -4.8) * mm, "construction": true});
            skCircle(sketch, "E168", {"center": v(-17.81, 0) * mm, "radius": 3.5 * mm});
            skSolve(sketch);
        }
        {
            var Q0;
            Q0=makeQuery(id+"F4.imprint","IMPRINT",FACE,{"disambiguationData":[TD([[makeQuery(id+"F4.imprint","IMPRINT",EDGE,{"derivedFrom":sQuery(id+"F4.wireOp",EDGE,"E168")}),1.0]])]});
            extrude(context, id + "F5", {"entities" : qUnion([Q0]), "oppositeDirection" : true, "depth" : 18 * mm, "offsetDistance" : 25 * mm, "hasSecondDirection" : true, "secondDirectionOppositeDirection" : false, "secondDirectionDepth" : 1 * mm});
        }
        {
            var Q0;
            Q0=qCreatedBy(makeId("Front.planeOp"),FACE);
            var sketch = newSketch(context, id + "F6", { "sketchPlane" : qUnion([Q0])});
            skLineSegment(sketch, "E169", {"start": v(0, -73.39) * mm, "end": v(0, 72.36) * mm, "construction": true});
            skSolve(sketch);
        }
        {
            var Q0;
            Q0=makeQuery(id+"F5.opExtrude","SWEPT_BODY",BODY,{"disambiguationData":[OSD([sQuery(id+"F4.wireOp",EDGE,"E168")])]});
            var Q1;
            Q1=sQuery(id+"F6.wireOp",EDGE,"E169");
            circularPattern(context, id + "F7", {"operationType" : NewBodyOperationType.REMOVE, "entities" : qUnion([Q0]), "axis" : qUnion([Q1]), "angle" : 360 * degree, "instanceCount" : 3, "equalSpace" : true});
        }
        {
            var Q0;
            Q0=makeQuery(id+"F1.opExtrude","SWEPT_FACE",FACE,{"disambiguationData":[OSD([sQuery(id+"F0.wireOp",EDGE,"E148")])]});
            var sketch = newSketch(context, id + "F8", { "sketchPlane" : qUnion([Q0])});
            skLineSegment(sketch, "E170", {"start": v(-17.28, 0) * mm, "end": v(-6.72, 0) * mm, "construction": true});
            skLineSegment(sketch, "E171", {"start": v(-12, 4.8) * mm, "end": v(-12, -4.8) * mm, "construction": true});
            skCircle(sketch, "E172", {"center": v(-12, 0) * mm, "radius": 3.5 * mm});
            skSolve(sketch);
        }
        {
            var Q0;
            Q0=makeQuery(id+"F8.imprint","IMPRINT",FACE,{"disambiguationData":[TD([[makeQuery(id+"F8.imprint","IMPRINT",EDGE,{"derivedFrom":sQuery(id+"F8.wireOp",EDGE,"E172")}),1.0]])]});
            extrude(context, id + "F9", {"entities" : qUnion([Q0]), "oppositeDirection" : true, "depth" : 18 * mm, "offsetDistance" : 25 * mm, "hasSecondDirection" : true, "secondDirectionOppositeDirection" : false, "secondDirectionDepth" : 1 * mm});
        }
        {
            var Q0;
            Q0=makeQuery(id+"F9.opExtrude","SWEPT_BODY",BODY,{"disambiguationData":[OSD([sQuery(id+"F8.wireOp",EDGE,"E172")])]});
            var Q1;
            Q1=sQuery(id+"F6.wireOp",EDGE,"E169");
            circularPattern(context, id + "F10", {"operationType" : NewBodyOperationType.REMOVE, "entities" : qUnion([Q0]), "axis" : qUnion([Q1]), "angle" : 360 * degree, "instanceCount" : 3, "equalSpace" : true});
        }
        {
            var Q0;
            Q0=makeQuery(id+"F1.opExtrude","SWEPT_FACE",FACE,{"disambiguationData":[OSD([sQuery(id+"F0.wireOp",EDGE,"E0")])]});
            var sketch = newSketch(context, id + "F11", { "sketchPlane" : qUnion([Q0])});
            skLineSegment(sketch, "E173", {"start": v(-11.64, 0) * mm, "end": v(-1, 0) * mm, "construction": true});
            skLineSegment(sketch, "E174", {"start": v(-6.31, 4.8) * mm, "end": v(-6.31, -4.8) * mm, "construction": true});
            skCircle(sketch, "E175", {"center": v(-6.31, 0) * mm, "radius": 3.5 * mm});
            skSolve(sketch);
        }
        {
            var Q0;
            Q0=makeQuery(id+"F11.imprint","IMPRINT",FACE,{"disambiguationData":[TD([[makeQuery(id+"F11.imprint","IMPRINT",EDGE,{"derivedFrom":sQuery(id+"F11.wireOp",EDGE,"E175")}),1.0]])]});
            extrude(context, id + "F12", {"entities" : qUnion([Q0]), "oppositeDirection" : true, "depth" : 18 * mm, "offsetDistance" : 25 * mm, "hasSecondDirection" : true, "secondDirectionOppositeDirection" : false, "secondDirectionDepth" : 1 * mm});
        }
        {
            var Q0;
            Q0=makeQuery(id+"F12.opExtrude","SWEPT_BODY",BODY,{"disambiguationData":[OSD([sQuery(id+"F11.wireOp",EDGE,"E175")])]});
            var Q1;
            Q1=sQuery(id+"F6.wireOp",EDGE,"E169");
            circularPattern(context, id + "F13", {"operationType" : NewBodyOperationType.REMOVE, "entities" : qUnion([Q0]), "axis" : qUnion([Q1]), "angle" : 360 * degree, "instanceCount" : 3, "equalSpace" : true});
        }
        {
            var Q0;
            Q0=makeQuery(id+"F7.boolean.opBoolean","INTERSECT",EDGE,{"derivedFrom":[makeQuery(id+"F1.opExtrude","SWEPT_FACE",FACE,{"disambiguationData":[OSD([sQuery(id+"F0.wireOp",EDGE,"E131")])]}),makeQuery(id+"F7.opPattern","COPY",FACE,{"derivedFrom":makeQuery(id+"F5.opExtrude","SWEPT_FACE",FACE,{"disambiguationData":[OSD([sQuery(id+"F4.wireOp",EDGE,"E168")])]}),"instanceName":"1"})]});
            var Q1;
            Q1=makeQuery(id+"F10.boolean.opBoolean","INTERSECT",EDGE,{"derivedFrom":[makeQuery(id+"F1.opExtrude","SWEPT_FACE",FACE,{"disambiguationData":[OSD([sQuery(id+"F0.wireOp",EDGE,"E148")])]}),makeQuery(id+"F9.opExtrude","SWEPT_FACE",FACE,{"disambiguationData":[OSD([sQuery(id+"F8.wireOp",EDGE,"E172")])]})]});
            var Q2;
            Q2=makeQuery(id+"F13.boolean.opBoolean","INTERSECT",EDGE,{"derivedFrom":[makeQuery(id+"F1.opExtrude","SWEPT_FACE",FACE,{"disambiguationData":[OSD([sQuery(id+"F0.wireOp",EDGE,"E0")])]}),makeQuery(id+"F12.opExtrude","SWEPT_FACE",FACE,{"disambiguationData":[OSD([sQuery(id+"F11.wireOp",EDGE,"E175")])]})]});
            var Q3;
            Q3=makeQuery(id+"F7.boolean.opBoolean","INTERSECT",EDGE,{"derivedFrom":[makeQuery(id+"F1.opExtrude","SWEPT_FACE",FACE,{"disambiguationData":[OSD([sQuery(id+"F0.wireOp",EDGE,"E21")])]}),makeQuery(id+"F7.opPattern","COPY",FACE,{"derivedFrom":makeQuery(id+"F5.opExtrude","SWEPT_FACE",FACE,{"disambiguationData":[OSD([sQuery(id+"F4.wireOp",EDGE,"E168")])]}),"instanceName":"2"})]});
            var Q4;
            Q4=makeQuery(id+"F10.boolean.opBoolean","INTERSECT",EDGE,{"derivedFrom":[makeQuery(id+"F1.opExtrude","SWEPT_FACE",FACE,{"disambiguationData":[OSD([sQuery(id+"F0.wireOp",EDGE,"E38")])]}),makeQuery(id+"F10.opPattern","COPY",FACE,{"derivedFrom":makeQuery(id+"F9.opExtrude","SWEPT_FACE",FACE,{"disambiguationData":[OSD([sQuery(id+"F8.wireOp",EDGE,"E172")])]}),"instanceName":"1"})]});
            var Q5;
            Q5=makeQuery(id+"F13.boolean.opBoolean","INTERSECT",EDGE,{"derivedFrom":[makeQuery(id+"F1.opExtrude","SWEPT_FACE",FACE,{"disambiguationData":[OSD([sQuery(id+"F0.wireOp",EDGE,"E55")])]}),makeQuery(id+"F13.opPattern","COPY",FACE,{"derivedFrom":makeQuery(id+"F12.opExtrude","SWEPT_FACE",FACE,{"disambiguationData":[OSD([sQuery(id+"F11.wireOp",EDGE,"E175")])]}),"instanceName":"1"})]});
            var Q6;
            Q6=makeQuery(id+"F7.boolean.opBoolean","INTERSECT",EDGE,{"derivedFrom":[makeQuery(id+"F1.opExtrude","SWEPT_FACE",FACE,{"disambiguationData":[OSD([sQuery(id+"F0.wireOp",EDGE,"E76")])]}),makeQuery(id+"F5.opExtrude","SWEPT_FACE",FACE,{"disambiguationData":[OSD([sQuery(id+"F4.wireOp",EDGE,"E168")])]})]});
            var Q7;
            Q7=makeQuery(id+"F10.boolean.opBoolean","INTERSECT",EDGE,{"derivedFrom":[makeQuery(id+"F1.opExtrude","SWEPT_FACE",FACE,{"disambiguationData":[OSD([sQuery(id+"F0.wireOp",EDGE,"E93")])]}),makeQuery(id+"F10.opPattern","COPY",FACE,{"derivedFrom":makeQuery(id+"F9.opExtrude","SWEPT_FACE",FACE,{"disambiguationData":[OSD([sQuery(id+"F8.wireOp",EDGE,"E172")])]}),"instanceName":"2"})]});
            var Q8;
            Q8=makeQuery(id+"F13.boolean.opBoolean","INTERSECT",EDGE,{"derivedFrom":[makeQuery(id+"F1.opExtrude","SWEPT_FACE",FACE,{"disambiguationData":[OSD([sQuery(id+"F0.wireOp",EDGE,"E110")])]}),makeQuery(id+"F13.opPattern","COPY",FACE,{"derivedFrom":makeQuery(id+"F12.opExtrude","SWEPT_FACE",FACE,{"disambiguationData":[OSD([sQuery(id+"F11.wireOp",EDGE,"E175")])]}),"instanceName":"2"})]});
            chamfer(context, id + "F14", {"entities" : qUnion([Q0, Q1, Q2, Q3, Q4, Q5, Q6, Q7, Q8]), "width" : 0.5 * mm, "tangentPropagation" : true});
        }
        {
            var Q0;
            Q0=makeQuery(id+"F1.opExtrude","SWEPT_BODY",BODY,{"disambiguationData":[OSD([sQuery(id+"F0.wireOp",EDGE,"E0"),sQuery(id+"F0.wireOp",EDGE,"E1"),sQuery(id+"F0.wireOp",EDGE,"E2"),sQuery(id+"F0.wireOp",EDGE,"E3"),sQuery(id+"F0.wireOp",EDGE,"E4"),sQuery(id+"F0.wireOp",EDGE,"E5"),sQuery(id+"F0.wireOp",EDGE,"E6"),sQuery(id+"F0.wireOp",EDGE,"E7"),sQuery(id+"F0.wireOp",EDGE,"E8"),sQuery(id+"F0.wireOp",EDGE,"E9"),sQuery(id+"F0.wireOp",EDGE,"E10"),sQuery(id+"F0.wireOp",EDGE,"E11"),sQuery(id+"F0.wireOp",EDGE,"E12"),sQuery(id+"F0.wireOp",EDGE,"E13"),sQuery(id+"F0.wireOp",EDGE,"E14"),sQuery(id+"F0.wireOp",EDGE,"E15"),sQuery(id+"F0.wireOp",EDGE,"E16"),sQuery(id+"F0.wireOp",EDGE,"E17"),sQuery(id+"F0.wireOp",EDGE,"E18"),sQuery(id+"F0.wireOp",EDGE,"E19"),sQuery(id+"F0.wireOp",EDGE,"E20"),sQuery(id+"F0.wireOp",EDGE,"E21"),sQuery(id+"F0.wireOp",EDGE,"E22"),sQuery(id+"F0.wireOp",EDGE,"E23"),sQuery(id+"F0.wireOp",EDGE,"E24"),sQuery(id+"F0.wireOp",EDGE,"E25"),sQuery(id+"F0.wireOp",EDGE,"E26"),sQuery(id+"F0.wireOp",EDGE,"E27"),sQuery(id+"F0.wireOp",EDGE,"E28"),sQuery(id+"F0.wireOp",EDGE,"E29"),sQuery(id+"F0.wireOp",EDGE,"E30"),sQuery(id+"F0.wireOp",EDGE,"E31"),sQuery(id+"F0.wireOp",EDGE,"E32"),sQuery(id+"F0.wireOp",EDGE,"E33"),sQuery(id+"F0.wireOp",EDGE,"E34"),sQuery(id+"F0.wireOp",EDGE,"E35"),sQuery(id+"F0.wireOp",EDGE,"E36"),sQuery(id+"F0.wireOp",EDGE,"E37"),sQuery(id+"F0.wireOp",EDGE,"E38"),sQuery(id+"F0.wireOp",EDGE,"E39"),sQuery(id+"F0.wireOp",EDGE,"E40"),sQuery(id+"F0.wireOp",EDGE,"E41"),sQuery(id+"F0.wireOp",EDGE,"E42"),sQuery(id+"F0.wireOp",EDGE,"E43"),sQuery(id+"F0.wireOp",EDGE,"E44"),sQuery(id+"F0.wireOp",EDGE,"E45"),sQuery(id+"F0.wireOp",EDGE,"E46"),sQuery(id+"F0.wireOp",EDGE,"E47"),sQuery(id+"F0.wireOp",EDGE,"E48"),sQuery(id+"F0.wireOp",EDGE,"E49"),sQuery(id+"F0.wireOp",EDGE,"E50"),sQuery(id+"F0.wireOp",EDGE,"E51"),sQuery(id+"F0.wireOp",EDGE,"E52"),sQuery(id+"F0.wireOp",EDGE,"E53"),sQuery(id+"F0.wireOp",EDGE,"E54"),sQuery(id+"F0.wireOp",EDGE,"E55"),sQuery(id+"F0.wireOp",EDGE,"E56"),sQuery(id+"F0.wireOp",EDGE,"E57"),sQuery(id+"F0.wireOp",EDGE,"E58"),sQuery(id+"F0.wireOp",EDGE,"E59"),sQuery(id+"F0.wireOp",EDGE,"E60"),sQuery(id+"F0.wireOp",EDGE,"E61"),sQuery(id+"F0.wireOp",EDGE,"E62"),sQuery(id+"F0.wireOp",EDGE,"E63"),sQuery(id+"F0.wireOp",EDGE,"E64"),sQuery(id+"F0.wireOp",EDGE,"E65"),sQuery(id+"F0.wireOp",EDGE,"E66"),sQuery(id+"F0.wireOp",EDGE,"E67"),sQuery(id+"F0.wireOp",EDGE,"E68"),sQuery(id+"F0.wireOp",EDGE,"E69"),sQuery(id+"F0.wireOp",EDGE,"E70"),sQuery(id+"F0.wireOp",EDGE,"E71"),sQuery(id+"F0.wireOp",EDGE,"E72"),sQuery(id+"F0.wireOp",EDGE,"E73"),sQuery(id+"F0.wireOp",EDGE,"E74"),sQuery(id+"F0.wireOp",EDGE,"E75"),sQuery(id+"F0.wireOp",EDGE,"E76"),sQuery(id+"F0.wireOp",EDGE,"E77"),sQuery(id+"F0.wireOp",EDGE,"E78"),sQuery(id+"F0.wireOp",EDGE,"E79"),sQuery(id+"F0.wireOp",EDGE,"E80"),sQuery(id+"F0.wireOp",EDGE,"E81"),sQuery(id+"F0.wireOp",EDGE,"E82"),sQuery(id+"F0.wireOp",EDGE,"E83"),sQuery(id+"F0.wireOp",EDGE,"E84"),sQuery(id+"F0.wireOp",EDGE,"E85"),sQuery(id+"F0.wireOp",EDGE,"E86"),sQuery(id+"F0.wireOp",EDGE,"E87"),sQuery(id+"F0.wireOp",EDGE,"E88"),sQuery(id+"F0.wireOp",EDGE,"E89"),sQuery(id+"F0.wireOp",EDGE,"E90"),sQuery(id+"F0.wireOp",EDGE,"E91"),sQuery(id+"F0.wireOp",EDGE,"E92"),sQuery(id+"F0.wireOp",EDGE,"E93"),sQuery(id+"F0.wireOp",EDGE,"E94"),sQuery(id+"F0.wireOp",EDGE,"E95"),sQuery(id+"F0.wireOp",EDGE,"E96"),sQuery(id+"F0.wireOp",EDGE,"E97"),sQuery(id+"F0.wireOp",EDGE,"E98"),sQuery(id+"F0.wireOp",EDGE,"E99"),sQuery(id+"F0.wireOp",EDGE,"E100"),sQuery(id+"F0.wireOp",EDGE,"E101"),sQuery(id+"F0.wireOp",EDGE,"E102"),sQuery(id+"F0.wireOp",EDGE,"E103"),sQuery(id+"F0.wireOp",EDGE,"E104"),sQuery(id+"F0.wireOp",EDGE,"E105"),sQuery(id+"F0.wireOp",EDGE,"E106"),sQuery(id+"F0.wireOp",EDGE,"E107"),sQuery(id+"F0.wireOp",EDGE,"E108"),sQuery(id+"F0.wireOp",EDGE,"E109"),sQuery(id+"F0.wireOp",EDGE,"E110"),sQuery(id+"F0.wireOp",EDGE,"E111"),sQuery(id+"F0.wireOp",EDGE,"E112"),sQuery(id+"F0.wireOp",EDGE,"E113"),sQuery(id+"F0.wireOp",EDGE,"E114"),sQuery(id+"F0.wireOp",EDGE,"E115"),sQuery(id+"F0.wireOp",EDGE,"E116"),sQuery(id+"F0.wireOp",EDGE,"E117"),sQuery(id+"F0.wireOp",EDGE,"E118"),sQuery(id+"F0.wireOp",EDGE,"E119"),sQuery(id+"F0.wireOp",EDGE,"E120"),sQuery(id+"F0.wireOp",EDGE,"E121"),sQuery(id+"F0.wireOp",EDGE,"E122"),sQuery(id+"F0.wireOp",EDGE,"E123"),sQuery(id+"F0.wireOp",EDGE,"E124"),sQuery(id+"F0.wireOp",EDGE,"E125"),sQuery(id+"F0.wireOp",EDGE,"E126"),sQuery(id+"F0.wireOp",EDGE,"E127"),sQuery(id+"F0.wireOp",EDGE,"E128"),sQuery(id+"F0.wireOp",EDGE,"E129"),sQuery(id+"F0.wireOp",EDGE,"E130"),sQuery(id+"F0.wireOp",EDGE,"E131"),sQuery(id+"F0.wireOp",EDGE,"E132"),sQuery(id+"F0.wireOp",EDGE,"E133"),sQuery(id+"F0.wireOp",EDGE,"E134"),sQuery(id+"F0.wireOp",EDGE,"E135"),sQuery(id+"F0.wireOp",EDGE,"E136"),sQuery(id+"F0.wireOp",EDGE,"E137"),sQuery(id+"F0.wireOp",EDGE,"E138"),sQuery(id+"F0.wireOp",EDGE,"E139"),sQuery(id+"F0.wireOp",EDGE,"E140"),sQuery(id+"F0.wireOp",EDGE,"E141"),sQuery(id+"F0.wireOp",EDGE,"E142"),sQuery(id+"F0.wireOp",EDGE,"E143"),sQuery(id+"F0.wireOp",EDGE,"E144"),sQuery(id+"F0.wireOp",EDGE,"E145"),sQuery(id+"F0.wireOp",EDGE,"E146"),sQuery(id+"F0.wireOp",EDGE,"E147"),sQuery(id+"F0.wireOp",EDGE,"E148"),sQuery(id+"F0.wireOp",EDGE,"E149"),sQuery(id+"F0.wireOp",EDGE,"E150"),sQuery(id+"F0.wireOp",EDGE,"E151"),sQuery(id+"F0.wireOp",EDGE,"E152"),sQuery(id+"F0.wireOp",EDGE,"E153"),sQuery(id+"F0.wireOp",EDGE,"E154"),sQuery(id+"F0.wireOp",EDGE,"E155"),sQuery(id+"F0.wireOp",EDGE,"E156"),sQuery(id+"F0.wireOp",EDGE,"E157"),sQuery(id+"F0.wireOp",EDGE,"E158"),sQuery(id+"F0.wireOp",EDGE,"E159"),sQuery(id+"F0.wireOp",EDGE,"E160"),sQuery(id+"F0.wireOp",EDGE,"E161"),sQuery(id+"F0.wireOp",EDGE,"E162"),sQuery(id+"F0.wireOp",EDGE,"E163"),sQuery(id+"F0.wireOp",EDGE,"E164")])]});
            var Q1;
            Q1=qCreatedBy(makeId("Origin.pointOp"),VERTEX);
            transform(context, id + "F15", {"entities" : qUnion([Q0]), "transformType" : TransformType.SCALE_UNIFORMLY, "scale" : 0.85, "scalePoint" : qUnion([Q1]), "makeCopy" : false});
        }
        {
            var Q0;
            Q0=qCreatedBy(makeId("Top.planeOp"),FACE);
            var sketch = newSketch(context, id + "F16", { "sketchPlane" : qUnion([Q0])});
            skCircle(sketch, "E176", {"center": v(0, 0) * mm, "radius": 11 * mm});
            skSolve(sketch);
        }
        {
            var Q0;
            Q0=makeQuery(id+"F16.imprint","IMPRINT",FACE,{"disambiguationData":[TD([[makeQuery(id+"F16.imprint","IMPRINT",EDGE,{"derivedFrom":sQuery(id+"F16.wireOp",EDGE,"E176")}),1.0]])]});
            extrude(context, id + "F17", {"entities" : qUnion([Q0]), "operationType" : NewBodyOperationType.REMOVE, "endBound" : BoundingType.SYMMETRIC, "depth" : 11 * mm, "offsetDistance" : 25 * mm});
        }
        {
            var Q0;
            Q0=makeQuery(id+"F17.boolean.opBoolean","INTERSECT",EDGE,{"derivedFrom":[makeQuery(id+"F1.opExtrude","CAP_FACE",FACE,{"disambiguationData":[OSD([sQuery(id+"F0.wireOp",EDGE,"E0"),sQuery(id+"F0.wireOp",EDGE,"E1"),sQuery(id+"F0.wireOp",EDGE,"E2"),sQuery(id+"F0.wireOp",EDGE,"E3"),sQuery(id+"F0.wireOp",EDGE,"E4"),sQuery(id+"F0.wireOp",EDGE,"E5"),sQuery(id+"F0.wireOp",EDGE,"E6"),sQuery(id+"F0.wireOp",EDGE,"E7"),sQuery(id+"F0.wireOp",EDGE,"E8"),sQuery(id+"F0.wireOp",EDGE,"E9"),sQuery(id+"F0.wireOp",EDGE,"E10"),sQuery(id+"F0.wireOp",EDGE,"E11"),sQuery(id+"F0.wireOp",EDGE,"E12"),sQuery(id+"F0.wireOp",EDGE,"E13"),sQuery(id+"F0.wireOp",EDGE,"E14"),sQuery(id+"F0.wireOp",EDGE,"E15"),sQuery(id+"F0.wireOp",EDGE,"E16"),sQuery(id+"F0.wireOp",EDGE,"E17"),sQuery(id+"F0.wireOp",EDGE,"E18"),sQuery(id+"F0.wireOp",EDGE,"E19"),sQuery(id+"F0.wireOp",EDGE,"E20"),sQuery(id+"F0.wireOp",EDGE,"E21"),sQuery(id+"F0.wireOp",EDGE,"E22"),sQuery(id+"F0.wireOp",EDGE,"E23"),sQuery(id+"F0.wireOp",EDGE,"E24"),sQuery(id+"F0.wireOp",EDGE,"E25"),sQuery(id+"F0.wireOp",EDGE,"E26"),sQuery(id+"F0.wireOp",EDGE,"E27"),sQuery(id+"F0.wireOp",EDGE,"E28"),sQuery(id+"F0.wireOp",EDGE,"E29"),sQuery(id+"F0.wireOp",EDGE,"E30"),sQuery(id+"F0.wireOp",EDGE,"E31"),sQuery(id+"F0.wireOp",EDGE,"E32"),sQuery(id+"F0.wireOp",EDGE,"E33"),sQuery(id+"F0.wireOp",EDGE,"E34"),sQuery(id+"F0.wireOp",EDGE,"E35"),sQuery(id+"F0.wireOp",EDGE,"E36"),sQuery(id+"F0.wireOp",EDGE,"E37"),sQuery(id+"F0.wireOp",EDGE,"E38"),sQuery(id+"F0.wireOp",EDGE,"E39"),sQuery(id+"F0.wireOp",EDGE,"E40"),sQuery(id+"F0.wireOp",EDGE,"E41"),sQuery(id+"F0.wireOp",EDGE,"E42"),sQuery(id+"F0.wireOp",EDGE,"E43"),sQuery(id+"F0.wireOp",EDGE,"E44"),sQuery(id+"F0.wireOp",EDGE,"E45"),sQuery(id+"F0.wireOp",EDGE,"E46"),sQuery(id+"F0.wireOp",EDGE,"E47"),sQuery(id+"F0.wireOp",EDGE,"E48"),sQuery(id+"F0.wireOp",EDGE,"E49"),sQuery(id+"F0.wireOp",EDGE,"E50"),sQuery(id+"F0.wireOp",EDGE,"E51"),sQuery(id+"F0.wireOp",EDGE,"E52"),sQuery(id+"F0.wireOp",EDGE,"E53"),sQuery(id+"F0.wireOp",EDGE,"E54"),sQuery(id+"F0.wireOp",EDGE,"E55"),sQuery(id+"F0.wireOp",EDGE,"E56"),sQuery(id+"F0.wireOp",EDGE,"E57"),sQuery(id+"F0.wireOp",EDGE,"E58"),sQuery(id+"F0.wireOp",EDGE,"E59"),sQuery(id+"F0.wireOp",EDGE,"E60"),sQuery(id+"F0.wireOp",EDGE,"E61"),sQuery(id+"F0.wireOp",EDGE,"E62"),sQuery(id+"F0.wireOp",EDGE,"E63"),sQuery(id+"F0.wireOp",EDGE,"E64"),sQuery(id+"F0.wireOp",EDGE,"E65"),sQuery(id+"F0.wireOp",EDGE,"E66"),sQuery(id+"F0.wireOp",EDGE,"E67"),sQuery(id+"F0.wireOp",EDGE,"E68"),sQuery(id+"F0.wireOp",EDGE,"E69"),sQuery(id+"F0.wireOp",EDGE,"E70"),sQuery(id+"F0.wireOp",EDGE,"E71"),sQuery(id+"F0.wireOp",EDGE,"E72"),sQuery(id+"F0.wireOp",EDGE,"E73"),sQuery(id+"F0.wireOp",EDGE,"E74"),sQuery(id+"F0.wireOp",EDGE,"E75"),sQuery(id+"F0.wireOp",EDGE,"E76"),sQuery(id+"F0.wireOp",EDGE,"E77"),sQuery(id+"F0.wireOp",EDGE,"E78"),sQuery(id+"F0.wireOp",EDGE,"E79"),sQuery(id+"F0.wireOp",EDGE,"E80"),sQuery(id+"F0.wireOp",EDGE,"E81"),sQuery(id+"F0.wireOp",EDGE,"E82"),sQuery(id+"F0.wireOp",EDGE,"E83"),sQuery(id+"F0.wireOp",EDGE,"E84"),sQuery(id+"F0.wireOp",EDGE,"E85"),sQuery(id+"F0.wireOp",EDGE,"E86"),sQuery(id+"F0.wireOp",EDGE,"E87"),sQuery(id+"F0.wireOp",EDGE,"E88"),sQuery(id+"F0.wireOp",EDGE,"E89"),sQuery(id+"F0.wireOp",EDGE,"E90"),sQuery(id+"F0.wireOp",EDGE,"E91"),sQuery(id+"F0.wireOp",EDGE,"E92"),sQuery(id+"F0.wireOp",EDGE,"E93"),sQuery(id+"F0.wireOp",EDGE,"E94"),sQuery(id+"F0.wireOp",EDGE,"E95"),sQuery(id+"F0.wireOp",EDGE,"E96"),sQuery(id+"F0.wireOp",EDGE,"E97"),sQuery(id+"F0.wireOp",EDGE,"E98"),sQuery(id+"F0.wireOp",EDGE,"E99"),sQuery(id+"F0.wireOp",EDGE,"E100"),sQuery(id+"F0.wireOp",EDGE,"E101"),sQuery(id+"F0.wireOp",EDGE,"E102"),sQuery(id+"F0.wireOp",EDGE,"E103"),sQuery(id+"F0.wireOp",EDGE,"E104"),sQuery(id+"F0.wireOp",EDGE,"E105"),sQuery(id+"F0.wireOp",EDGE,"E106"),sQuery(id+"F0.wireOp",EDGE,"E107"),sQuery(id+"F0.wireOp",EDGE,"E108"),sQuery(id+"F0.wireOp",EDGE,"E109"),sQuery(id+"F0.wireOp",EDGE,"E110"),sQuery(id+"F0.wireOp",EDGE,"E111"),sQuery(id+"F0.wireOp",EDGE,"E112"),sQuery(id+"F0.wireOp",EDGE,"E113"),sQuery(id+"F0.wireOp",EDGE,"E114"),sQuery(id+"F0.wireOp",EDGE,"E115"),sQuery(id+"F0.wireOp",EDGE,"E116"),sQuery(id+"F0.wireOp",EDGE,"E117"),sQuery(id+"F0.wireOp",EDGE,"E118"),sQuery(id+"F0.wireOp",EDGE,"E119"),sQuery(id+"F0.wireOp",EDGE,"E120"),sQuery(id+"F0.wireOp",EDGE,"E121"),sQuery(id+"F0.wireOp",EDGE,"E122"),sQuery(id+"F0.wireOp",EDGE,"E123"),sQuery(id+"F0.wireOp",EDGE,"E124"),sQuery(id+"F0.wireOp",EDGE,"E125"),sQuery(id+"F0.wireOp",EDGE,"E126"),sQuery(id+"F0.wireOp",EDGE,"E127"),sQuery(id+"F0.wireOp",EDGE,"E128"),sQuery(id+"F0.wireOp",EDGE,"E129"),sQuery(id+"F0.wireOp",EDGE,"E130"),sQuery(id+"F0.wireOp",EDGE,"E131"),sQuery(id+"F0.wireOp",EDGE,"E132"),sQuery(id+"F0.wireOp",EDGE,"E133"),sQuery(id+"F0.wireOp",EDGE,"E134"),sQuery(id+"F0.wireOp",EDGE,"E135"),sQuery(id+"F0.wireOp",EDGE,"E136"),sQuery(id+"F0.wireOp",EDGE,"E137"),sQuery(id+"F0.wireOp",EDGE,"E138"),sQuery(id+"F0.wireOp",EDGE,"E139"),sQuery(id+"F0.wireOp",EDGE,"E140"),sQuery(id+"F0.wireOp",EDGE,"E141"),sQuery(id+"F0.wireOp",EDGE,"E142"),sQuery(id+"F0.wireOp",EDGE,"E143"),sQuery(id+"F0.wireOp",EDGE,"E144"),sQuery(id+"F0.wireOp",EDGE,"E145"),sQuery(id+"F0.wireOp",EDGE,"E146"),sQuery(id+"F0.wireOp",EDGE,"E147"),sQuery(id+"F0.wireOp",EDGE,"E148"),sQuery(id+"F0.wireOp",EDGE,"E149"),sQuery(id+"F0.wireOp",EDGE,"E150"),sQuery(id+"F0.wireOp",EDGE,"E151"),sQuery(id+"F0.wireOp",EDGE,"E152"),sQuery(id+"F0.wireOp",EDGE,"E153"),sQuery(id+"F0.wireOp",EDGE,"E154"),sQuery(id+"F0.wireOp",EDGE,"E155"),sQuery(id+"F0.wireOp",EDGE,"E156"),sQuery(id+"F0.wireOp",EDGE,"E157"),sQuery(id+"F0.wireOp",EDGE,"E158"),sQuery(id+"F0.wireOp",EDGE,"E159"),sQuery(id+"F0.wireOp",EDGE,"E160"),sQuery(id+"F0.wireOp",EDGE,"E161"),sQuery(id+"F0.wireOp",EDGE,"E162"),sQuery(id+"F0.wireOp",EDGE,"E163"),sQuery(id+"F0.wireOp",EDGE,"E164")])],"isStart":false}),makeQuery(id+"F17.opExtrude","SWEPT_FACE",FACE,{"disambiguationData":[OSD([sQuery(id+"F16.wireOp",EDGE,"E176")])]})]});
            var Q1;
            Q1=makeQuery(id+"F17.boolean.opBoolean","INTERSECT",EDGE,{"derivedFrom":[makeQuery(id+"F1.opExtrude","CAP_FACE",FACE,{"disambiguationData":[OSD([sQuery(id+"F0.wireOp",EDGE,"E0"),sQuery(id+"F0.wireOp",EDGE,"E1"),sQuery(id+"F0.wireOp",EDGE,"E2"),sQuery(id+"F0.wireOp",EDGE,"E3"),sQuery(id+"F0.wireOp",EDGE,"E4"),sQuery(id+"F0.wireOp",EDGE,"E5"),sQuery(id+"F0.wireOp",EDGE,"E6"),sQuery(id+"F0.wireOp",EDGE,"E7"),sQuery(id+"F0.wireOp",EDGE,"E8"),sQuery(id+"F0.wireOp",EDGE,"E9"),sQuery(id+"F0.wireOp",EDGE,"E10"),sQuery(id+"F0.wireOp",EDGE,"E11"),sQuery(id+"F0.wireOp",EDGE,"E12"),sQuery(id+"F0.wireOp",EDGE,"E13"),sQuery(id+"F0.wireOp",EDGE,"E14"),sQuery(id+"F0.wireOp",EDGE,"E15"),sQuery(id+"F0.wireOp",EDGE,"E16"),sQuery(id+"F0.wireOp",EDGE,"E17"),sQuery(id+"F0.wireOp",EDGE,"E18"),sQuery(id+"F0.wireOp",EDGE,"E19"),sQuery(id+"F0.wireOp",EDGE,"E20"),sQuery(id+"F0.wireOp",EDGE,"E21"),sQuery(id+"F0.wireOp",EDGE,"E22"),sQuery(id+"F0.wireOp",EDGE,"E23"),sQuery(id+"F0.wireOp",EDGE,"E24"),sQuery(id+"F0.wireOp",EDGE,"E25"),sQuery(id+"F0.wireOp",EDGE,"E26"),sQuery(id+"F0.wireOp",EDGE,"E27"),sQuery(id+"F0.wireOp",EDGE,"E28"),sQuery(id+"F0.wireOp",EDGE,"E29"),sQuery(id+"F0.wireOp",EDGE,"E30"),sQuery(id+"F0.wireOp",EDGE,"E31"),sQuery(id+"F0.wireOp",EDGE,"E32"),sQuery(id+"F0.wireOp",EDGE,"E33"),sQuery(id+"F0.wireOp",EDGE,"E34"),sQuery(id+"F0.wireOp",EDGE,"E35"),sQuery(id+"F0.wireOp",EDGE,"E36"),sQuery(id+"F0.wireOp",EDGE,"E37"),sQuery(id+"F0.wireOp",EDGE,"E38"),sQuery(id+"F0.wireOp",EDGE,"E39"),sQuery(id+"F0.wireOp",EDGE,"E40"),sQuery(id+"F0.wireOp",EDGE,"E41"),sQuery(id+"F0.wireOp",EDGE,"E42"),sQuery(id+"F0.wireOp",EDGE,"E43"),sQuery(id+"F0.wireOp",EDGE,"E44"),sQuery(id+"F0.wireOp",EDGE,"E45"),sQuery(id+"F0.wireOp",EDGE,"E46"),sQuery(id+"F0.wireOp",EDGE,"E47"),sQuery(id+"F0.wireOp",EDGE,"E48"),sQuery(id+"F0.wireOp",EDGE,"E49"),sQuery(id+"F0.wireOp",EDGE,"E50"),sQuery(id+"F0.wireOp",EDGE,"E51"),sQuery(id+"F0.wireOp",EDGE,"E52"),sQuery(id+"F0.wireOp",EDGE,"E53"),sQuery(id+"F0.wireOp",EDGE,"E54"),sQuery(id+"F0.wireOp",EDGE,"E55"),sQuery(id+"F0.wireOp",EDGE,"E56"),sQuery(id+"F0.wireOp",EDGE,"E57"),sQuery(id+"F0.wireOp",EDGE,"E58"),sQuery(id+"F0.wireOp",EDGE,"E59"),sQuery(id+"F0.wireOp",EDGE,"E60"),sQuery(id+"F0.wireOp",EDGE,"E61"),sQuery(id+"F0.wireOp",EDGE,"E62"),sQuery(id+"F0.wireOp",EDGE,"E63"),sQuery(id+"F0.wireOp",EDGE,"E64"),sQuery(id+"F0.wireOp",EDGE,"E65"),sQuery(id+"F0.wireOp",EDGE,"E66"),sQuery(id+"F0.wireOp",EDGE,"E67"),sQuery(id+"F0.wireOp",EDGE,"E68"),sQuery(id+"F0.wireOp",EDGE,"E69"),sQuery(id+"F0.wireOp",EDGE,"E70"),sQuery(id+"F0.wireOp",EDGE,"E71"),sQuery(id+"F0.wireOp",EDGE,"E72"),sQuery(id+"F0.wireOp",EDGE,"E73"),sQuery(id+"F0.wireOp",EDGE,"E74"),sQuery(id+"F0.wireOp",EDGE,"E75"),sQuery(id+"F0.wireOp",EDGE,"E76"),sQuery(id+"F0.wireOp",EDGE,"E77"),sQuery(id+"F0.wireOp",EDGE,"E78"),sQuery(id+"F0.wireOp",EDGE,"E79"),sQuery(id+"F0.wireOp",EDGE,"E80"),sQuery(id+"F0.wireOp",EDGE,"E81"),sQuery(id+"F0.wireOp",EDGE,"E82"),sQuery(id+"F0.wireOp",EDGE,"E83"),sQuery(id+"F0.wireOp",EDGE,"E84"),sQuery(id+"F0.wireOp",EDGE,"E85"),sQuery(id+"F0.wireOp",EDGE,"E86"),sQuery(id+"F0.wireOp",EDGE,"E87"),sQuery(id+"F0.wireOp",EDGE,"E88"),sQuery(id+"F0.wireOp",EDGE,"E89"),sQuery(id+"F0.wireOp",EDGE,"E90"),sQuery(id+"F0.wireOp",EDGE,"E91"),sQuery(id+"F0.wireOp",EDGE,"E92"),sQuery(id+"F0.wireOp",EDGE,"E93"),sQuery(id+"F0.wireOp",EDGE,"E94"),sQuery(id+"F0.wireOp",EDGE,"E95"),sQuery(id+"F0.wireOp",EDGE,"E96"),sQuery(id+"F0.wireOp",EDGE,"E97"),sQuery(id+"F0.wireOp",EDGE,"E98"),sQuery(id+"F0.wireOp",EDGE,"E99"),sQuery(id+"F0.wireOp",EDGE,"E100"),sQuery(id+"F0.wireOp",EDGE,"E101"),sQuery(id+"F0.wireOp",EDGE,"E102"),sQuery(id+"F0.wireOp",EDGE,"E103"),sQuery(id+"F0.wireOp",EDGE,"E104"),sQuery(id+"F0.wireOp",EDGE,"E105"),sQuery(id+"F0.wireOp",EDGE,"E106"),sQuery(id+"F0.wireOp",EDGE,"E107"),sQuery(id+"F0.wireOp",EDGE,"E108"),sQuery(id+"F0.wireOp",EDGE,"E109"),sQuery(id+"F0.wireOp",EDGE,"E110"),sQuery(id+"F0.wireOp",EDGE,"E111"),sQuery(id+"F0.wireOp",EDGE,"E112"),sQuery(id+"F0.wireOp",EDGE,"E113"),sQuery(id+"F0.wireOp",EDGE,"E114"),sQuery(id+"F0.wireOp",EDGE,"E115"),sQuery(id+"F0.wireOp",EDGE,"E116"),sQuery(id+"F0.wireOp",EDGE,"E117"),sQuery(id+"F0.wireOp",EDGE,"E118"),sQuery(id+"F0.wireOp",EDGE,"E119"),sQuery(id+"F0.wireOp",EDGE,"E120"),sQuery(id+"F0.wireOp",EDGE,"E121"),sQuery(id+"F0.wireOp",EDGE,"E122"),sQuery(id+"F0.wireOp",EDGE,"E123"),sQuery(id+"F0.wireOp",EDGE,"E124"),sQuery(id+"F0.wireOp",EDGE,"E125"),sQuery(id+"F0.wireOp",EDGE,"E126"),sQuery(id+"F0.wireOp",EDGE,"E127"),sQuery(id+"F0.wireOp",EDGE,"E128"),sQuery(id+"F0.wireOp",EDGE,"E129"),sQuery(id+"F0.wireOp",EDGE,"E130"),sQuery(id+"F0.wireOp",EDGE,"E131"),sQuery(id+"F0.wireOp",EDGE,"E132"),sQuery(id+"F0.wireOp",EDGE,"E133"),sQuery(id+"F0.wireOp",EDGE,"E134"),sQuery(id+"F0.wireOp",EDGE,"E135"),sQuery(id+"F0.wireOp",EDGE,"E136"),sQuery(id+"F0.wireOp",EDGE,"E137"),sQuery(id+"F0.wireOp",EDGE,"E138"),sQuery(id+"F0.wireOp",EDGE,"E139"),sQuery(id+"F0.wireOp",EDGE,"E140"),sQuery(id+"F0.wireOp",EDGE,"E141"),sQuery(id+"F0.wireOp",EDGE,"E142"),sQuery(id+"F0.wireOp",EDGE,"E143"),sQuery(id+"F0.wireOp",EDGE,"E144"),sQuery(id+"F0.wireOp",EDGE,"E145"),sQuery(id+"F0.wireOp",EDGE,"E146"),sQuery(id+"F0.wireOp",EDGE,"E147"),sQuery(id+"F0.wireOp",EDGE,"E148"),sQuery(id+"F0.wireOp",EDGE,"E149"),sQuery(id+"F0.wireOp",EDGE,"E150"),sQuery(id+"F0.wireOp",EDGE,"E151"),sQuery(id+"F0.wireOp",EDGE,"E152"),sQuery(id+"F0.wireOp",EDGE,"E153"),sQuery(id+"F0.wireOp",EDGE,"E154"),sQuery(id+"F0.wireOp",EDGE,"E155"),sQuery(id+"F0.wireOp",EDGE,"E156"),sQuery(id+"F0.wireOp",EDGE,"E157"),sQuery(id+"F0.wireOp",EDGE,"E158"),sQuery(id+"F0.wireOp",EDGE,"E159"),sQuery(id+"F0.wireOp",EDGE,"E160"),sQuery(id+"F0.wireOp",EDGE,"E161"),sQuery(id+"F0.wireOp",EDGE,"E162"),sQuery(id+"F0.wireOp",EDGE,"E163"),sQuery(id+"F0.wireOp",EDGE,"E164")])],"isStart":true}),makeQuery(id+"F17.opExtrude","SWEPT_FACE",FACE,{"disambiguationData":[OSD([sQuery(id+"F16.wireOp",EDGE,"E176")])]})]});
            chamfer(context, id + "F18", {"entities" : qUnion([Q0, Q1]), "width" : 1.6 * mm, "tangentPropagation" : true});
        }
    });
